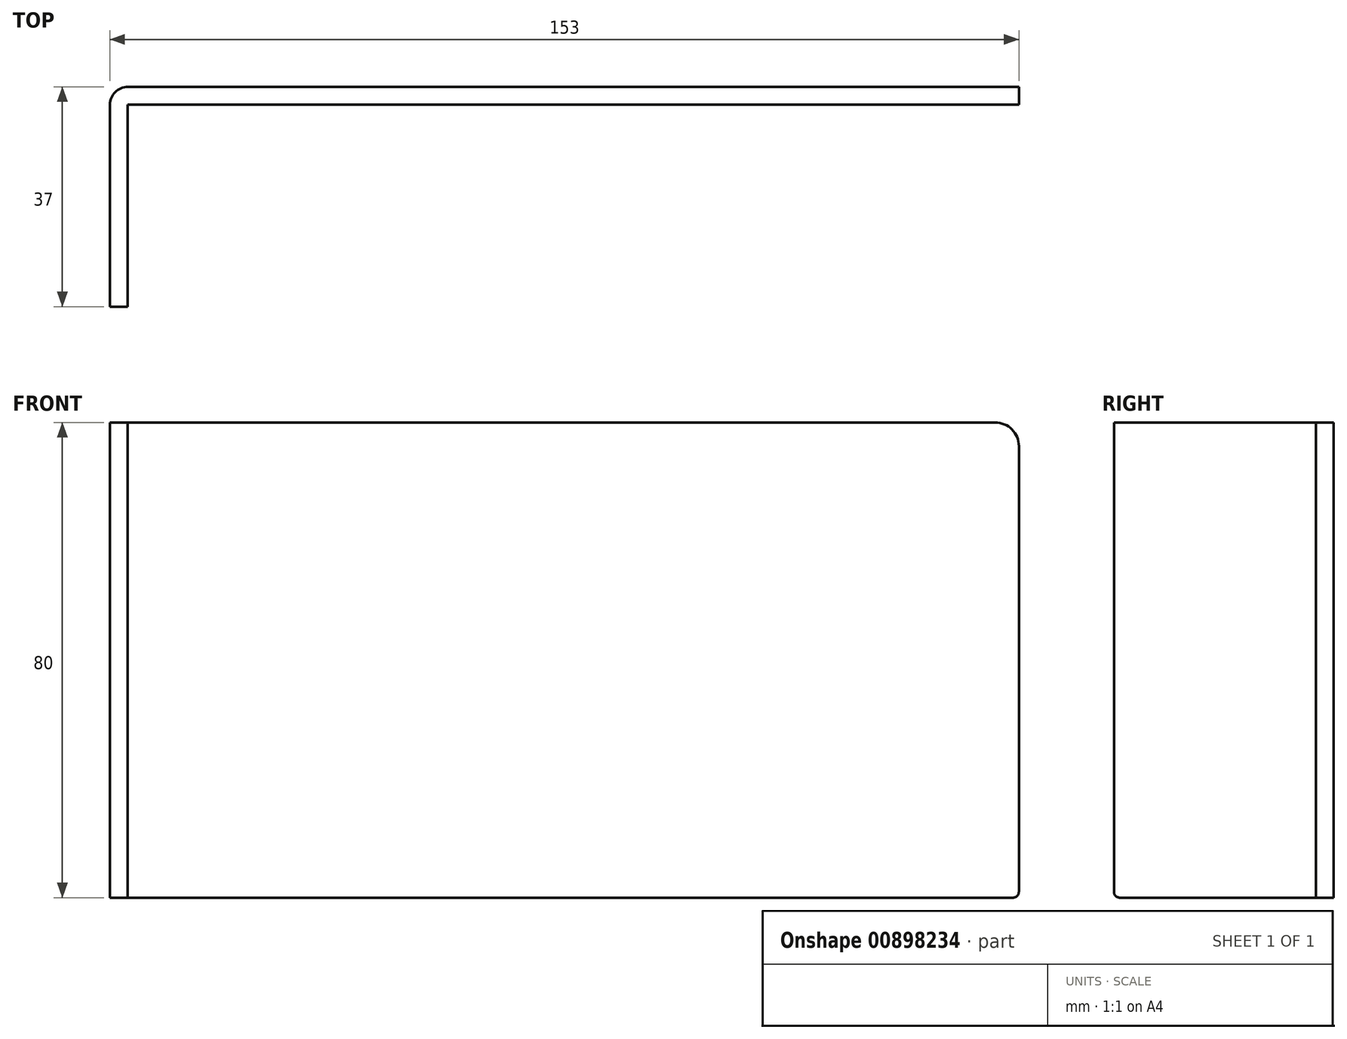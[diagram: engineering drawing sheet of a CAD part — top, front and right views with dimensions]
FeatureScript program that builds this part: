
annotation { "Feature Type Name" : "Feature", "Feature Type Description" : "" }
export const myFeature = defineFeature(function(context is Context, id is Id, definition is map)
    precondition{}
    {
        {
            var Q0;
            Q0=qCreatedBy(makeId("Front.planeOp"),FACE);
            var sketch = newSketch(context, id + "F0", { "sketchPlane" : qUnion([Q0])});
            skLineSegment(sketch, "E0.bottom", {"start": v(0, 0) * mm, "end": v(153, 0) * mm});
            skLineSegment(sketch, "E0.top", {"start": v(0, 80) * mm, "end": v(149, 80) * mm});
            skLineSegment(sketch, "E0.left", {"start": v(0, 0) * mm, "end": v(0, 80) * mm});
            skLineSegment(sketch, "E0.right", {"start": v(153, 0) * mm, "end": v(153, 76) * mm});
            skPoint(sketch, "E1.visualSharp", {"position": v(153, 80) * mm});
            skArc(sketch, "E1.filletArc", {"start": v(153, 76) * mm, "mid": v(151.83, 78.83) * mm, "end": v(149, 80) * mm});
            skSolve(sketch);
        }
        {
            var Q0;
            Q0=qSketchRegion(id+"F0",true);
            extrude(context, id + "F1", {"entities" : qUnion([Q0]), "endBound" : BoundingType.SYMMETRIC, "depth" : 3 * mm});
        }
        {
            var Q0;
            Q0=makeQuery(id+"F1.opExtrude","CAP_FACE",FACE,{"disambiguationData":[OSD([sQuery(id+"F0.wireOp",EDGE,"E0.bottom"),sQuery(id+"F0.wireOp",EDGE,"E0.top"),sQuery(id+"F0.wireOp",EDGE,"E0.left"),sQuery(id+"F0.wireOp",EDGE,"E0.right"),sQuery(id+"F0.wireOp",EDGE,"E1.filletArc")])],"isStart":false});
            var sketch = newSketch(context, id + "F2", { "sketchPlane" : qUnion([Q0])});
            skLineSegment(sketch, "E2", {"start": v(0, 0) * mm, "end": v(0, 80) * mm});
            skLineSegment(sketch, "E3", {"start": v(0, 80) * mm, "end": v(3, 80) * mm});
            skLineSegment(sketch, "E4", {"start": v(3, 80) * mm, "end": v(3, 0) * mm});
            skLineSegment(sketch, "E5", {"start": v(3, 0) * mm, "end": v(0, 0) * mm});
            skSolve(sketch);
        }
        {
            var Q0;
            Q0=qSketchRegion(id+"F2",true);
            extrude(context, id + "F3", {"entities" : qUnion([Q0]), "operationType" : NewBodyOperationType.ADD, "depth" : 34 * mm});
        }
        {
            var Q0;
            Q0=makeQuery(id+"F1.opExtrude","CAP_EDGE",EDGE,{"disambiguationData":[OSD([sQuery(id+"F0.wireOp",EDGE,"E0.left")])],"isStart":true});
            fillet(context, id + "F4", {"entities" : qUnion([Q0]), "radius" : 3 * mm, "tangentPropagation" : true, "allowEdgeOverflow" : false});
        }
        {
            var Q0;
            Q0=makeQuery(id+"F3.opExtrude","CAP_EDGE",EDGE,{"disambiguationData":[OSD([sQuery(id+"F2.wireOp",EDGE,"E5")])],"isStart":false});
            var Q1;
            Q1=makeQuery(id+"F1.opExtrude","SWEPT_EDGE",EDGE,{"disambiguationData":[OSD([sQuery(id+"F0.wireOp",EDGE,"E0.bottom"),sQuery(id+"F0.wireOp",EDGE,"E0.right")])]});
            fillet(context, id + "F5", {"entities" : qUnion([Q0, Q1]), "radius" : 1 * mm, "tangentPropagation" : true, "allowEdgeOverflow" : false});
        }
    });
